annotation { "Feature Type Name" : "Feature", "Feature Type Description" : "" }
export const myFeature = defineFeature(function(context is Context, id is Id, definition is map)
    precondition{}
    {
        {
            var Q0;
            Q0=qCreatedBy(makeId("Front.planeOp"),FACE);
            var sketch = newSketch(context, id + "F0", { "sketchPlane" : qUnion([Q0])});
            skArc(sketch, "E0", {"start": v(0, -43.05) * mm, "mid": v(45.49, 1.39) * mm, "end": v(0, 45.82) * mm});
            skLineSegment(sketch, "E1", {"start": v(0, -43.05) * mm, "end": v(0, 45.82) * mm});
            skSolve(sketch);
        }
        {
            var Q0;
            Q0=makeQuery(id+"F0.imprint","IMPRINT",FACE,{"disambiguationData":[TD([[makeQuery(id+"F0.imprint","IMPRINT",EDGE,{"derivedFrom":sQuery(id+"F0.wireOp",EDGE,"E0")}),1.0]])]});
            var Q1;
            Q1=sQuery(id+"F0.wireOp",EDGE,"E1");
            revolve(context, id + "F1", {"entities" : qUnion([Q0]), "axis" : qUnion([Q1]), "revolveType" : RevolveType.FULL});
        }
        {
            var Q0;
            Q0=qCreatedBy(makeId("Right.planeOp"),FACE);
            cPlane(context, id + "F2", {"entities" : qUnion([Q0]), "cplaneType" : CPlaneType.OFFSET, "offset" : 46.6 * mm, "width" : 152.4 * mm, "height" : 152.4 * mm});
        }
        {
            var Q0;
            Q0=qCreatedBy(id+"F2.planeOp",FACE);
            var sketch = newSketch(context, id + "F3", { "sketchPlane" : qUnion([Q0])});
            skCircle(sketch, "E2", {"center": v(0, 0) * mm, "radius": 15.7 * mm});
            skSolve(sketch);
        }
        {
            var Q0;
            Q0=makeQuery(id+"F3.imprint","IMPRINT",FACE,{"disambiguationData":[TD([[makeQuery(id+"F3.imprint","IMPRINT",EDGE,{"derivedFrom":sQuery(id+"F3.wireOp",EDGE,"E2")}),1.0]])]});
            extrude(context, id + "F4", {"entities" : qUnion([Q0]), "operationType" : NewBodyOperationType.REMOVE, "oppositeDirection" : true, "depth" : 6.35 * mm});
        }
        {
            var Q0;
            Q0=makeQuery(id+"F4.boolean.opBoolean","COPY",FACE,{"derivedFrom":makeQuery(id+"F4.opExtrude","CAP_FACE",FACE,{"disambiguationData":[OSD([sQuery(id+"F3.wireOp",EDGE,"E2")])],"isStart":false})});
            var sketch = newSketch(context, id + "F5", { "sketchPlane" : qUnion([Q0])});
            skCircle(sketch, "E3", {"center": v(0, 0) * mm, "radius": 11.41 * mm});
            skCircle(sketch, "E4", {"center": v(0, 0) * mm, "radius": 7.45 * mm});
            skSolve(sketch);
        }
        {
            var Q0;
            Q0=makeQuery(id+"F5.imprint","IMPRINT",FACE,{"disambiguationData":[TD([[makeQuery(id+"F5.imprint","IMPRINT",EDGE,{"derivedFrom":sQuery(id+"F5.wireOp",EDGE,"E3")}),1.0]])]});
            extrude(context, id + "F6", {"entities" : qUnion([Q0]), "operationType" : NewBodyOperationType.ADD, "depth" : 3.8 * mm});
        }
        {
            var Q0;
            Q0=makeQuery(id+"F6.boolean.opBoolean","SPLIT",FACE,{"disambiguationData":[TD([makeQuery(id+"F6.opExtrude","SWEPT_FACE",FACE,{"disambiguationData":[OSD([sQuery(id+"F5.wireOp",EDGE,"E4")])]})])],"derivedFrom":makeQuery(id+"F4.boolean.opBoolean","COPY",FACE,{"derivedFrom":makeQuery(id+"F4.opExtrude","CAP_FACE",FACE,{"disambiguationData":[OSD([sQuery(id+"F3.wireOp",EDGE,"E2")])],"isStart":false})})});
            extrude(context, id + "F7", {"entities" : qUnion([Q0]), "operationType" : NewBodyOperationType.ADD, "depth" : 4.44 * mm});
        }
        {
            var Q0;
            Q0=qCreatedBy(id+"F2.planeOp",FACE);
            var sketch = newSketch(context, id + "F8", { "sketchPlane" : qUnion([Q0])});
            skText(sketch, "E5", { "text": "Lock Ball", "fontName": "OpenSans-BoldItalic.ttf"});
            const initialGuessF8  = {"E5": [-0.027, 0.02004, 1, 0, 0.00829]};
            skSetInitialGuess(sketch, initialGuessF8);
            skSolve(sketch);
        }
        {
            var Q0;
            Q0 = qSketchRegion(id + "F8", true);
            extrude(context, id + "F9", {"entities" : qUnion([Q0]), "operationType" : NewBodyOperationType.REMOVE, "oppositeDirection" : true, "depth" : 25.4 * mm});
        }
        {
            var Q0;
            Q0=qCreatedBy(id+"F2.planeOp",FACE);
            var sketch = newSketch(context, id + "F10", { "sketchPlane" : qUnion([Q0])});
            skLineSegment(sketch, "E6.bottom", {"start": v(-4.1, 36.36) * mm, "end": v(4.36, 36.36) * mm});
            skLineSegment(sketch, "E6.top", {"start": v(-4.1, 28.8) * mm, "end": v(4.36, 28.8) * mm});
            skLineSegment(sketch, "E6.left", {"start": v(-4.1, 36.36) * mm, "end": v(-4.1, 28.8) * mm});
            skLineSegment(sketch, "E6.right", {"start": v(4.36, 36.36) * mm, "end": v(4.36, 28.8) * mm});
            skArc(sketch, "E7", {"start": v(4.36, 36.36) * mm, "mid": v(0.13, 40.6) * mm, "end": v(-4.1, 36.36) * mm});
            skSolve(sketch);
        }
        {
            var Q0;
            Q0=makeQuery(id+"F10.imprint","IMPRINT",FACE,{"disambiguationData":[TD([[makeQuery(id+"F10.imprint","IMPRINT",EDGE,{"derivedFrom":sQuery(id+"F10.wireOp",EDGE,"E6.bottom")}),1.0]])]});
            var Q1;
            Q1=makeQuery(id+"F10.imprint","IMPRINT",FACE,{"disambiguationData":[TD([[makeQuery(id+"F10.imprint","IMPRINT",EDGE,{"derivedFrom":sQuery(id+"F10.wireOp",EDGE,"E6.bottom")}),-1.0]])]});
            extrude(context, id + "F11", {"entities" : qUnion([Q0, Q1]), "operationType" : NewBodyOperationType.REMOVE, "oppositeDirection" : true, "depth" : 25.4 * mm});
        }
        {
            var Q0;
            Q0=qCreatedBy(id+"F2.planeOp",FACE);
            var sketch = newSketch(context, id + "F12", { "sketchPlane" : qUnion([Q0])});
            skLineSegment(sketch, "E8.bottom", {"start": v(-38.3, 6.5) * mm, "end": v(-19.8, 6.5) * mm});
            skLineSegment(sketch, "E8.top", {"start": v(-38.3, -6.05) * mm, "end": v(-19.8, -6.05) * mm});
            skLineSegment(sketch, "E8.left", {"start": v(-38.3, 6.5) * mm, "end": v(-38.3, -6.05) * mm});
            skLineSegment(sketch, "E8.right", {"start": v(-19.8, 6.5) * mm, "end": v(-19.8, -6.05) * mm});
            skLineSegment(sketch, "E9.bottom", {"start": v(19.8, 6.5) * mm, "end": v(39.84, 6.5) * mm});
            skLineSegment(sketch, "E9.top", {"start": v(19.8, -6.05) * mm, "end": v(39.84, -6.05) * mm});
            skLineSegment(sketch, "E9.left", {"start": v(19.8, 6.5) * mm, "end": v(19.8, -6.05) * mm});
            skLineSegment(sketch, "E9.right", {"start": v(39.84, 6.5) * mm, "end": v(39.84, -6.05) * mm});
            skSolve(sketch);
        }
        {
            var Q0;
            Q0=makeQuery(id+"F12.imprint","IMPRINT",FACE,{"disambiguationData":[TD([[makeQuery(id+"F12.imprint","IMPRINT",EDGE,{"derivedFrom":sQuery(id+"F12.wireOp",EDGE,"E8.bottom")}),-1.0]])]});
            var Q1;
            Q1=makeQuery(id+"F12.imprint","IMPRINT",FACE,{"disambiguationData":[TD([[makeQuery(id+"F12.imprint","IMPRINT",EDGE,{"derivedFrom":sQuery(id+"F12.wireOp",EDGE,"E9.bottom")}),-1.0]])]});
            extrude(context, id + "F13", {"entities" : qUnion([Q0, Q1]), "operationType" : NewBodyOperationType.REMOVE, "oppositeDirection" : true, "depth" : 12.7 * mm});
        }
        {
            var Q0;
            Q0=makeQuery(id+"F13.boolean.opBoolean","INTERSECT",EDGE,{"derivedFrom":[makeQuery(id+"F9.boolean.opBoolean","SPLIT",FACE,{"disambiguationData":[TD([makeQuery(id+"F4.boolean.opBoolean","COPY",FACE,{"derivedFrom":makeQuery(id+"F4.opExtrude","SWEPT_FACE",FACE,{"disambiguationData":[OSD([sQuery(id+"F3.wireOp",EDGE,"E2")])]})})])],"derivedFrom":makeQuery(id+"F1.opRevolve","SWEPT_FACE",FACE,{"disambiguationData":[OSD([sQuery(id+"F0.wireOp",EDGE,"E0")])]})}),makeQuery(id+"F13.opExtrude","SWEPT_FACE",FACE,{"disambiguationData":[OSD([sQuery(id+"F12.wireOp",EDGE,"E8.bottom")])]})]});
            var Q1;
            Q1=makeQuery(id+"F13.boolean.opBoolean","INTERSECT",EDGE,{"derivedFrom":[makeQuery(id+"F9.boolean.opBoolean","SPLIT",FACE,{"disambiguationData":[TD([makeQuery(id+"F4.boolean.opBoolean","COPY",FACE,{"derivedFrom":makeQuery(id+"F4.opExtrude","SWEPT_FACE",FACE,{"disambiguationData":[OSD([sQuery(id+"F3.wireOp",EDGE,"E2")])]})})])],"derivedFrom":makeQuery(id+"F1.opRevolve","SWEPT_FACE",FACE,{"disambiguationData":[OSD([sQuery(id+"F0.wireOp",EDGE,"E0")])]})}),makeQuery(id+"F13.opExtrude","SWEPT_FACE",FACE,{"disambiguationData":[OSD([sQuery(id+"F12.wireOp",EDGE,"E9.bottom")])]})]});
            var Q2;
            Q2=makeQuery(id+"F13.boolean.opBoolean","INTERSECT",EDGE,{"derivedFrom":[makeQuery(id+"F9.boolean.opBoolean","SPLIT",FACE,{"disambiguationData":[TD([makeQuery(id+"F4.boolean.opBoolean","COPY",FACE,{"derivedFrom":makeQuery(id+"F4.opExtrude","SWEPT_FACE",FACE,{"disambiguationData":[OSD([sQuery(id+"F3.wireOp",EDGE,"E2")])]})})])],"derivedFrom":makeQuery(id+"F1.opRevolve","SWEPT_FACE",FACE,{"disambiguationData":[OSD([sQuery(id+"F0.wireOp",EDGE,"E0")])]})}),makeQuery(id+"F13.opExtrude","SWEPT_FACE",FACE,{"disambiguationData":[OSD([sQuery(id+"F12.wireOp",EDGE,"E9.top")])]})]});
            var Q3;
            Q3=makeQuery(id+"F13.boolean.opBoolean","INTERSECT",EDGE,{"derivedFrom":[makeQuery(id+"F9.boolean.opBoolean","SPLIT",FACE,{"disambiguationData":[TD([makeQuery(id+"F4.boolean.opBoolean","COPY",FACE,{"derivedFrom":makeQuery(id+"F4.opExtrude","SWEPT_FACE",FACE,{"disambiguationData":[OSD([sQuery(id+"F3.wireOp",EDGE,"E2")])]})})])],"derivedFrom":makeQuery(id+"F1.opRevolve","SWEPT_FACE",FACE,{"disambiguationData":[OSD([sQuery(id+"F0.wireOp",EDGE,"E0")])]})}),makeQuery(id+"F13.opExtrude","SWEPT_FACE",FACE,{"disambiguationData":[OSD([sQuery(id+"F12.wireOp",EDGE,"E8.top")])]})]});
            fillet(context, id + "F14", {"entities" : qUnion([Q0, Q1, Q2, Q3]), "radius" : 5.08 * mm, "tangentPropagation" : true, "allowEdgeOverflow" : false});
        }
        {
            var Q0;
            Q0=makeQuery(id+"F13.boolean.opBoolean","INTERSECT",EDGE,{"derivedFrom":[makeQuery(id+"F9.boolean.opBoolean","SPLIT",FACE,{"disambiguationData":[TD([makeQuery(id+"F4.boolean.opBoolean","COPY",FACE,{"derivedFrom":makeQuery(id+"F4.opExtrude","SWEPT_FACE",FACE,{"disambiguationData":[OSD([sQuery(id+"F3.wireOp",EDGE,"E2")])]})})])],"derivedFrom":makeQuery(id+"F1.opRevolve","SWEPT_FACE",FACE,{"disambiguationData":[OSD([sQuery(id+"F0.wireOp",EDGE,"E0")])]})}),makeQuery(id+"F13.opExtrude","CAP_FACE",FACE,{"disambiguationData":[OSD([sQuery(id+"F12.wireOp",EDGE,"E8.bottom"),sQuery(id+"F12.wireOp",EDGE,"E8.top"),sQuery(id+"F12.wireOp",EDGE,"E8.left"),sQuery(id+"F12.wireOp",EDGE,"E8.right")])],"isStart":false})]});
            var Q1;
            Q1=makeQuery(id+"F13.boolean.opBoolean","INTERSECT",EDGE,{"derivedFrom":[makeQuery(id+"F9.boolean.opBoolean","SPLIT",FACE,{"disambiguationData":[TD([makeQuery(id+"F4.boolean.opBoolean","COPY",FACE,{"derivedFrom":makeQuery(id+"F4.opExtrude","SWEPT_FACE",FACE,{"disambiguationData":[OSD([sQuery(id+"F3.wireOp",EDGE,"E2")])]})})])],"derivedFrom":makeQuery(id+"F1.opRevolve","SWEPT_FACE",FACE,{"disambiguationData":[OSD([sQuery(id+"F0.wireOp",EDGE,"E0")])]})}),makeQuery(id+"F13.opExtrude","CAP_FACE",FACE,{"disambiguationData":[OSD([sQuery(id+"F12.wireOp",EDGE,"E9.bottom"),sQuery(id+"F12.wireOp",EDGE,"E9.top"),sQuery(id+"F12.wireOp",EDGE,"E9.left"),sQuery(id+"F12.wireOp",EDGE,"E9.right")])],"isStart":false})]});
            chamfer(context, id + "F15", {"entities" : qUnion([Q0, Q1]), "width" : 5.08 * mm, "tangentPropagation" : true});
        }
        {
            var Q0;
            {var subQ0=makeQuery(id+"F13.opExtrude","CAP_FACE",FACE,{"disambiguationData":[OSD([sQuery(id+"F12.wireOp",EDGE,"E8.bottom"),sQuery(id+"F12.wireOp",EDGE,"E8.top"),sQuery(id+"F12.wireOp",EDGE,"E8.left"),sQuery(id+"F12.wireOp",EDGE,"E8.right")])],"isStart":false});Q0=makeQuery(id+"F15.opChamfer","BLEND_EDGE",EDGE,{"blendedFrom":[makeQuery(id+"F13.boolean.opBoolean","INTERSECT",EDGE,{"derivedFrom":[makeQuery(id+"F9.boolean.opBoolean","SPLIT",FACE,{"disambiguationData":[TD([makeQuery(id+"F4.boolean.opBoolean","COPY",FACE,{"derivedFrom":makeQuery(id+"F4.opExtrude","SWEPT_FACE",FACE,{"disambiguationData":[OSD([sQuery(id+"F3.wireOp",EDGE,"E2")])]})})])],"derivedFrom":makeQuery(id+"F1.opRevolve","SWEPT_FACE",FACE,{"disambiguationData":[OSD([sQuery(id+"F0.wireOp",EDGE,"E0")])]})}),subQ0]}),makeQuery(id+"F13.boolean.opBoolean","COPY",FACE,{"derivedFrom":subQ0})],"blendedInto":[makeQuery(id+"F13.boolean.opBoolean","COPY",FACE,{"derivedFrom":subQ0})]});}
            var Q1;
            {var subQ0=makeQuery(id+"F13.opExtrude","CAP_FACE",FACE,{"disambiguationData":[OSD([sQuery(id+"F12.wireOp",EDGE,"E9.bottom"),sQuery(id+"F12.wireOp",EDGE,"E9.top"),sQuery(id+"F12.wireOp",EDGE,"E9.left"),sQuery(id+"F12.wireOp",EDGE,"E9.right")])],"isStart":false});Q1=makeQuery(id+"F15.opChamfer","BLEND_EDGE",EDGE,{"blendedFrom":[makeQuery(id+"F13.boolean.opBoolean","INTERSECT",EDGE,{"derivedFrom":[makeQuery(id+"F9.boolean.opBoolean","SPLIT",FACE,{"disambiguationData":[TD([makeQuery(id+"F4.boolean.opBoolean","COPY",FACE,{"derivedFrom":makeQuery(id+"F4.opExtrude","SWEPT_FACE",FACE,{"disambiguationData":[OSD([sQuery(id+"F3.wireOp",EDGE,"E2")])]})})])],"derivedFrom":makeQuery(id+"F1.opRevolve","SWEPT_FACE",FACE,{"disambiguationData":[OSD([sQuery(id+"F0.wireOp",EDGE,"E0")])]})}),subQ0]}),makeQuery(id+"F13.boolean.opBoolean","COPY",FACE,{"derivedFrom":subQ0})],"blendedInto":[makeQuery(id+"F13.boolean.opBoolean","COPY",FACE,{"derivedFrom":subQ0})]});}
            fillet(context, id + "F16", {"entities" : qUnion([Q0, Q1]), "radius" : 5.08 * mm, "tangentPropagation" : true, "allowEdgeOverflow" : false});
        }
        {
            var Q0;
            Q0=makeQuery(id+"F7.opExtrude","CAP_EDGE",EDGE,{"disambiguationData":[OSD([sQuery(id+"F5.wireOp",EDGE,"E4")])],"isStart":false});
            fillet(context, id + "F17", {"entities" : qUnion([Q0]), "radius" : 5.08 * mm, "tangentPropagation" : true, "allowEdgeOverflow" : false});
        }
        {
            var Q0;
            Q0=makeQuery(id+"F4.boolean.opBoolean","INTERSECT",EDGE,{"derivedFrom":[makeQuery(id+"F1.opRevolve","SWEPT_FACE",FACE,{"disambiguationData":[OSD([sQuery(id+"F0.wireOp",EDGE,"E0")])]}),makeQuery(id+"F4.opExtrude","SWEPT_FACE",FACE,{"disambiguationData":[OSD([sQuery(id+"F3.wireOp",EDGE,"E2")])]})]});
            fillet(context, id + "F18", {"entities" : qUnion([Q0]), "radius" : 5.08 * mm, "tangentPropagation" : true, "allowEdgeOverflow" : false});
        }
        {
            var Q0;
            Q0=makeQuery(id+"F11.boolean.opBoolean","INTERSECT",EDGE,{"derivedFrom":[makeQuery(id+"F9.boolean.opBoolean","SPLIT",FACE,{"disambiguationData":[TD([makeQuery(id+"F4.boolean.opBoolean","COPY",FACE,{"derivedFrom":makeQuery(id+"F4.opExtrude","SWEPT_FACE",FACE,{"disambiguationData":[OSD([sQuery(id+"F3.wireOp",EDGE,"E2")])]})})])],"derivedFrom":makeQuery(id+"F1.opRevolve","SWEPT_FACE",FACE,{"disambiguationData":[OSD([sQuery(id+"F0.wireOp",EDGE,"E0")])]})}),makeQuery(id+"F11.opExtrude","SWEPT_FACE",FACE,{"disambiguationData":[OSD([sQuery(id+"F10.wireOp",EDGE,"E7")])]})]});
            fillet(context, id + "F19", {"entities" : qUnion([Q0]), "radius" : 5.08 * mm, "tangentPropagation" : true, "allowEdgeOverflow" : false});
        }
        {
            var Q0;
            Q0=makeQuery(id+"F11.boolean.opBoolean","COPY",FACE,{"derivedFrom":makeQuery(id+"F11.opExtrude","CAP_FACE",FACE,{"disambiguationData":[OSD([sQuery(id+"F10.wireOp",EDGE,"E6.top"),sQuery(id+"F10.wireOp",EDGE,"E6.left"),sQuery(id+"F10.wireOp",EDGE,"E6.right"),sQuery(id+"F10.wireOp",EDGE,"E7")])],"isStart":false})});
            extrude(context, id + "F20", {"entities" : qUnion([Q0]), "operationType" : NewBodyOperationType.ADD, "depth" : 5.08 * mm});
        }
        {
            var Q0;
            Q0=makeQuery(id+"F9.boolean.opBoolean","COPY",FACE,{"derivedFrom":makeQuery(id+"F9.opExtrude","CAP_FACE",FACE,{"disambiguationData":[OSD([sQuery(id+"F8.wireOp",EDGE,"E5.sketch_text.stroke-0"),sQuery(id+"F8.wireOp",EDGE,"E5.sketch_text.stroke-1"),sQuery(id+"F8.wireOp",EDGE,"E5.sketch_text.stroke-2"),sQuery(id+"F8.wireOp",EDGE,"E5.sketch_text.stroke-3"),sQuery(id+"F8.wireOp",EDGE,"E5.sketch_text.stroke-4"),sQuery(id+"F8.wireOp",EDGE,"E5.sketch_text.stroke-5")])],"isStart":false})});
            extrude(context, id + "F21", {"entities" : qUnion([Q0]), "operationType" : NewBodyOperationType.ADD, "depth" : 5.08 * mm});
        }
        {
            var Q0;
            Q0=makeQuery(id+"F9.boolean.opBoolean","COPY",FACE,{"derivedFrom":makeQuery(id+"F9.opExtrude","CAP_FACE",FACE,{"disambiguationData":[OSD([sQuery(id+"F8.wireOp",EDGE,"E5.sketch_text.stroke-6"),sQuery(id+"F8.wireOp",EDGE,"E5.sketch_text.stroke-7"),sQuery(id+"F8.wireOp",EDGE,"E5.sketch_text.stroke-8"),sQuery(id+"F8.wireOp",EDGE,"E5.sketch_text.stroke-9"),sQuery(id+"F8.wireOp",EDGE,"E5.sketch_text.stroke-10"),sQuery(id+"F8.wireOp",EDGE,"E5.sketch_text.stroke-11"),sQuery(id+"F8.wireOp",EDGE,"E5.sketch_text.stroke-12"),sQuery(id+"F8.wireOp",EDGE,"E5.sketch_text.stroke-13"),sQuery(id+"F8.wireOp",EDGE,"E5.sketch_text.stroke-14"),sQuery(id+"F8.wireOp",EDGE,"E5.sketch_text.stroke-15"),sQuery(id+"F8.wireOp",EDGE,"E5.sketch_text.stroke-16"),sQuery(id+"F8.wireOp",EDGE,"E5.sketch_text.stroke-17"),sQuery(id+"F8.wireOp",EDGE,"E5.sketch_text.stroke-18"),sQuery(id+"F8.wireOp",EDGE,"E5.sketch_text.stroke-19"),sQuery(id+"F8.wireOp",EDGE,"E5.sketch_text.stroke-20"),sQuery(id+"F8.wireOp",EDGE,"E5.sketch_text.stroke-21"),sQuery(id+"F8.wireOp",EDGE,"E5.sketch_text.stroke-22"),sQuery(id+"F8.wireOp",EDGE,"E5.sketch_text.stroke-23")])],"isStart":false})});
            extrude(context, id + "F22", {"entities" : qUnion([Q0]), "operationType" : NewBodyOperationType.ADD, "depth" : 2.54 * mm});
        }
        {
            var Q0;
            Q0=makeQuery(id+"F9.boolean.opBoolean","COPY",FACE,{"derivedFrom":makeQuery(id+"F9.opExtrude","CAP_FACE",FACE,{"disambiguationData":[OSD([sQuery(id+"F8.wireOp",EDGE,"E5.sketch_text.stroke-24"),sQuery(id+"F8.wireOp",EDGE,"E5.sketch_text.stroke-25"),sQuery(id+"F8.wireOp",EDGE,"E5.sketch_text.stroke-26"),sQuery(id+"F8.wireOp",EDGE,"E5.sketch_text.stroke-27"),sQuery(id+"F8.wireOp",EDGE,"E5.sketch_text.stroke-28"),sQuery(id+"F8.wireOp",EDGE,"E5.sketch_text.stroke-29"),sQuery(id+"F8.wireOp",EDGE,"E5.sketch_text.stroke-30"),sQuery(id+"F8.wireOp",EDGE,"E5.sketch_text.stroke-31"),sQuery(id+"F8.wireOp",EDGE,"E5.sketch_text.stroke-32"),sQuery(id+"F8.wireOp",EDGE,"E5.sketch_text.stroke-33"),sQuery(id+"F8.wireOp",EDGE,"E5.sketch_text.stroke-34"),sQuery(id+"F8.wireOp",EDGE,"E5.sketch_text.stroke-35"),sQuery(id+"F8.wireOp",EDGE,"E5.sketch_text.stroke-36"),sQuery(id+"F8.wireOp",EDGE,"E5.sketch_text.stroke-37"),sQuery(id+"F8.wireOp",EDGE,"E5.sketch_text.stroke-38"),sQuery(id+"F8.wireOp",EDGE,"E5.sketch_text.stroke-39"),sQuery(id+"F8.wireOp",EDGE,"E5.sketch_text.stroke-40"),sQuery(id+"F8.wireOp",EDGE,"E5.sketch_text.stroke-41")])],"isStart":false})});
            extrude(context, id + "F23", {"entities" : qUnion([Q0]), "operationType" : NewBodyOperationType.ADD, "depth" : 2.54 * mm});
        }
        {
            var Q0;
            Q0=makeQuery(id+"F9.boolean.opBoolean","COPY",FACE,{"derivedFrom":makeQuery(id+"F9.opExtrude","CAP_FACE",FACE,{"disambiguationData":[OSD([sQuery(id+"F8.wireOp",EDGE,"E5.sketch_text.stroke-42"),sQuery(id+"F8.wireOp",EDGE,"E5.sketch_text.stroke-43"),sQuery(id+"F8.wireOp",EDGE,"E5.sketch_text.stroke-44"),sQuery(id+"F8.wireOp",EDGE,"E5.sketch_text.stroke-45"),sQuery(id+"F8.wireOp",EDGE,"E5.sketch_text.stroke-46"),sQuery(id+"F8.wireOp",EDGE,"E5.sketch_text.stroke-47"),sQuery(id+"F8.wireOp",EDGE,"E5.sketch_text.stroke-48"),sQuery(id+"F8.wireOp",EDGE,"E5.sketch_text.stroke-49"),sQuery(id+"F8.wireOp",EDGE,"E5.sketch_text.stroke-50"),sQuery(id+"F8.wireOp",EDGE,"E5.sketch_text.stroke-51"),sQuery(id+"F8.wireOp",EDGE,"E5.sketch_text.stroke-52"),sQuery(id+"F8.wireOp",EDGE,"E5.sketch_text.stroke-53"),sQuery(id+"F8.wireOp",EDGE,"E5.sketch_text.stroke-54"),sQuery(id+"F8.wireOp",EDGE,"E5.sketch_text.stroke-55"),sQuery(id+"F8.wireOp",EDGE,"E5.sketch_text.stroke-56")])],"isStart":false})});
            extrude(context, id + "F24", {"entities" : qUnion([Q0]), "operationType" : NewBodyOperationType.ADD, "depth" : 2.54 * mm});
        }
        {
            var Q0;
            Q0=makeQuery(id+"F9.boolean.opBoolean","COPY",FACE,{"derivedFrom":makeQuery(id+"F9.opExtrude","CAP_FACE",FACE,{"disambiguationData":[OSD([sQuery(id+"F8.wireOp",EDGE,"E5.sketch_text.stroke-57"),sQuery(id+"F8.wireOp",EDGE,"E5.sketch_text.stroke-58"),sQuery(id+"F8.wireOp",EDGE,"E5.sketch_text.stroke-59"),sQuery(id+"F8.wireOp",EDGE,"E5.sketch_text.stroke-60"),sQuery(id+"F8.wireOp",EDGE,"E5.sketch_text.stroke-61"),sQuery(id+"F8.wireOp",EDGE,"E5.sketch_text.stroke-62"),sQuery(id+"F8.wireOp",EDGE,"E5.sketch_text.stroke-63"),sQuery(id+"F8.wireOp",EDGE,"E5.sketch_text.stroke-64"),sQuery(id+"F8.wireOp",EDGE,"E5.sketch_text.stroke-65"),sQuery(id+"F8.wireOp",EDGE,"E5.sketch_text.stroke-66"),sQuery(id+"F8.wireOp",EDGE,"E5.sketch_text.stroke-67"),sQuery(id+"F8.wireOp",EDGE,"E5.sketch_text.stroke-68"),sQuery(id+"F8.wireOp",EDGE,"E5.sketch_text.stroke-69"),sQuery(id+"F8.wireOp",EDGE,"E5.sketch_text.stroke-70"),sQuery(id+"F8.wireOp",EDGE,"E5.sketch_text.stroke-71"),sQuery(id+"F8.wireOp",EDGE,"E5.sketch_text.stroke-72"),sQuery(id+"F8.wireOp",EDGE,"E5.sketch_text.stroke-73"),sQuery(id+"F8.wireOp",EDGE,"E5.sketch_text.stroke-74"),sQuery(id+"F8.wireOp",EDGE,"E5.sketch_text.stroke-75"),sQuery(id+"F8.wireOp",EDGE,"E5.sketch_text.stroke-76"),sQuery(id+"F8.wireOp",EDGE,"E5.sketch_text.stroke-77"),sQuery(id+"F8.wireOp",EDGE,"E5.sketch_text.stroke-78"),sQuery(id+"F8.wireOp",EDGE,"E5.sketch_text.stroke-79"),sQuery(id+"F8.wireOp",EDGE,"E5.sketch_text.stroke-80")])],"isStart":false})});
            extrude(context, id + "F25", {"entities" : qUnion([Q0]), "operationType" : NewBodyOperationType.ADD, "depth" : 2.54 * mm});
        }
        {
            var Q0;
            Q0=makeQuery(id+"F9.boolean.opBoolean","COPY",FACE,{"derivedFrom":makeQuery(id+"F9.opExtrude","CAP_FACE",FACE,{"disambiguationData":[OSD([sQuery(id+"F8.wireOp",EDGE,"E5.sketch_text.stroke-81"),sQuery(id+"F8.wireOp",EDGE,"E5.sketch_text.stroke-82"),sQuery(id+"F8.wireOp",EDGE,"E5.sketch_text.stroke-83"),sQuery(id+"F8.wireOp",EDGE,"E5.sketch_text.stroke-84"),sQuery(id+"F8.wireOp",EDGE,"E5.sketch_text.stroke-85"),sQuery(id+"F8.wireOp",EDGE,"E5.sketch_text.stroke-86"),sQuery(id+"F8.wireOp",EDGE,"E5.sketch_text.stroke-87"),sQuery(id+"F8.wireOp",EDGE,"E5.sketch_text.stroke-88"),sQuery(id+"F8.wireOp",EDGE,"E5.sketch_text.stroke-89"),sQuery(id+"F8.wireOp",EDGE,"E5.sketch_text.stroke-90"),sQuery(id+"F8.wireOp",EDGE,"E5.sketch_text.stroke-91"),sQuery(id+"F8.wireOp",EDGE,"E5.sketch_text.stroke-92"),sQuery(id+"F8.wireOp",EDGE,"E5.sketch_text.stroke-93"),sQuery(id+"F8.wireOp",EDGE,"E5.sketch_text.stroke-94"),sQuery(id+"F8.wireOp",EDGE,"E5.sketch_text.stroke-95"),sQuery(id+"F8.wireOp",EDGE,"E5.sketch_text.stroke-96"),sQuery(id+"F8.wireOp",EDGE,"E5.sketch_text.stroke-97"),sQuery(id+"F8.wireOp",EDGE,"E5.sketch_text.stroke-98"),sQuery(id+"F8.wireOp",EDGE,"E5.sketch_text.stroke-99"),sQuery(id+"F8.wireOp",EDGE,"E5.sketch_text.stroke-100"),sQuery(id+"F8.wireOp",EDGE,"E5.sketch_text.stroke-101"),sQuery(id+"F8.wireOp",EDGE,"E5.sketch_text.stroke-102"),sQuery(id+"F8.wireOp",EDGE,"E5.sketch_text.stroke-103"),sQuery(id+"F8.wireOp",EDGE,"E5.sketch_text.stroke-104"),sQuery(id+"F8.wireOp",EDGE,"E5.sketch_text.stroke-105")])],"isStart":false})});
            extrude(context, id + "F26", {"entities" : qUnion([Q0]), "operationType" : NewBodyOperationType.ADD, "depth" : 2.54 * mm});
        }
        {
            var Q0;
            Q0=makeQuery(id+"F9.boolean.opBoolean","COPY",FACE,{"derivedFrom":makeQuery(id+"F9.opExtrude","CAP_FACE",FACE,{"disambiguationData":[OSD([sQuery(id+"F8.wireOp",EDGE,"E5.sketch_text.stroke-106"),sQuery(id+"F8.wireOp",EDGE,"E5.sketch_text.stroke-107"),sQuery(id+"F8.wireOp",EDGE,"E5.sketch_text.stroke-108"),sQuery(id+"F8.wireOp",EDGE,"E5.sketch_text.stroke-109")])],"isStart":false})});
            extrude(context, id + "F27", {"entities" : qUnion([Q0]), "operationType" : NewBodyOperationType.ADD, "depth" : 2.54 * mm});
        }
        {
            var Q0;
            Q0=makeQuery(id+"F27.opExtrude","CAP_FACE",FACE,{"disambiguationData":[OSD([sQuery(id+"F8.wireOp",EDGE,"E5.sketch_text.stroke-106"),sQuery(id+"F8.wireOp",EDGE,"E5.sketch_text.stroke-107"),sQuery(id+"F8.wireOp",EDGE,"E5.sketch_text.stroke-108"),sQuery(id+"F8.wireOp",EDGE,"E5.sketch_text.stroke-109")])],"isStart":false});
            extrude(context, id + "F28", {"entities" : qUnion([Q0]), "operationType" : NewBodyOperationType.ADD, "depth" : 2.54 * mm});
        }
        {
            var Q0;
            Q0=makeQuery(id+"F9.boolean.opBoolean","COPY",FACE,{"derivedFrom":makeQuery(id+"F9.opExtrude","CAP_FACE",FACE,{"disambiguationData":[OSD([sQuery(id+"F8.wireOp",EDGE,"E5.sketch_text.stroke-110"),sQuery(id+"F8.wireOp",EDGE,"E5.sketch_text.stroke-111"),sQuery(id+"F8.wireOp",EDGE,"E5.sketch_text.stroke-112"),sQuery(id+"F8.wireOp",EDGE,"E5.sketch_text.stroke-113")])],"isStart":false})});
            extrude(context, id + "F29", {"entities" : qUnion([Q0]), "operationType" : NewBodyOperationType.ADD, "depth" : 2.54 * mm});
        }
        {
            var Q0;
            Q0=makeQuery(id+"F20.opExtrude","CAP_FACE",FACE,{"disambiguationData":[OSD([sQuery(id+"F10.wireOp",EDGE,"E6.top"),sQuery(id+"F10.wireOp",EDGE,"E6.left"),sQuery(id+"F10.wireOp",EDGE,"E6.right"),sQuery(id+"F10.wireOp",EDGE,"E7")])],"isStart":false});
            extrude(context, id + "F30", {"entities" : qUnion([Q0]), "operationType" : NewBodyOperationType.REMOVE, "oppositeDirection" : true, "depth" : 5.05 * mm});
        }
    });